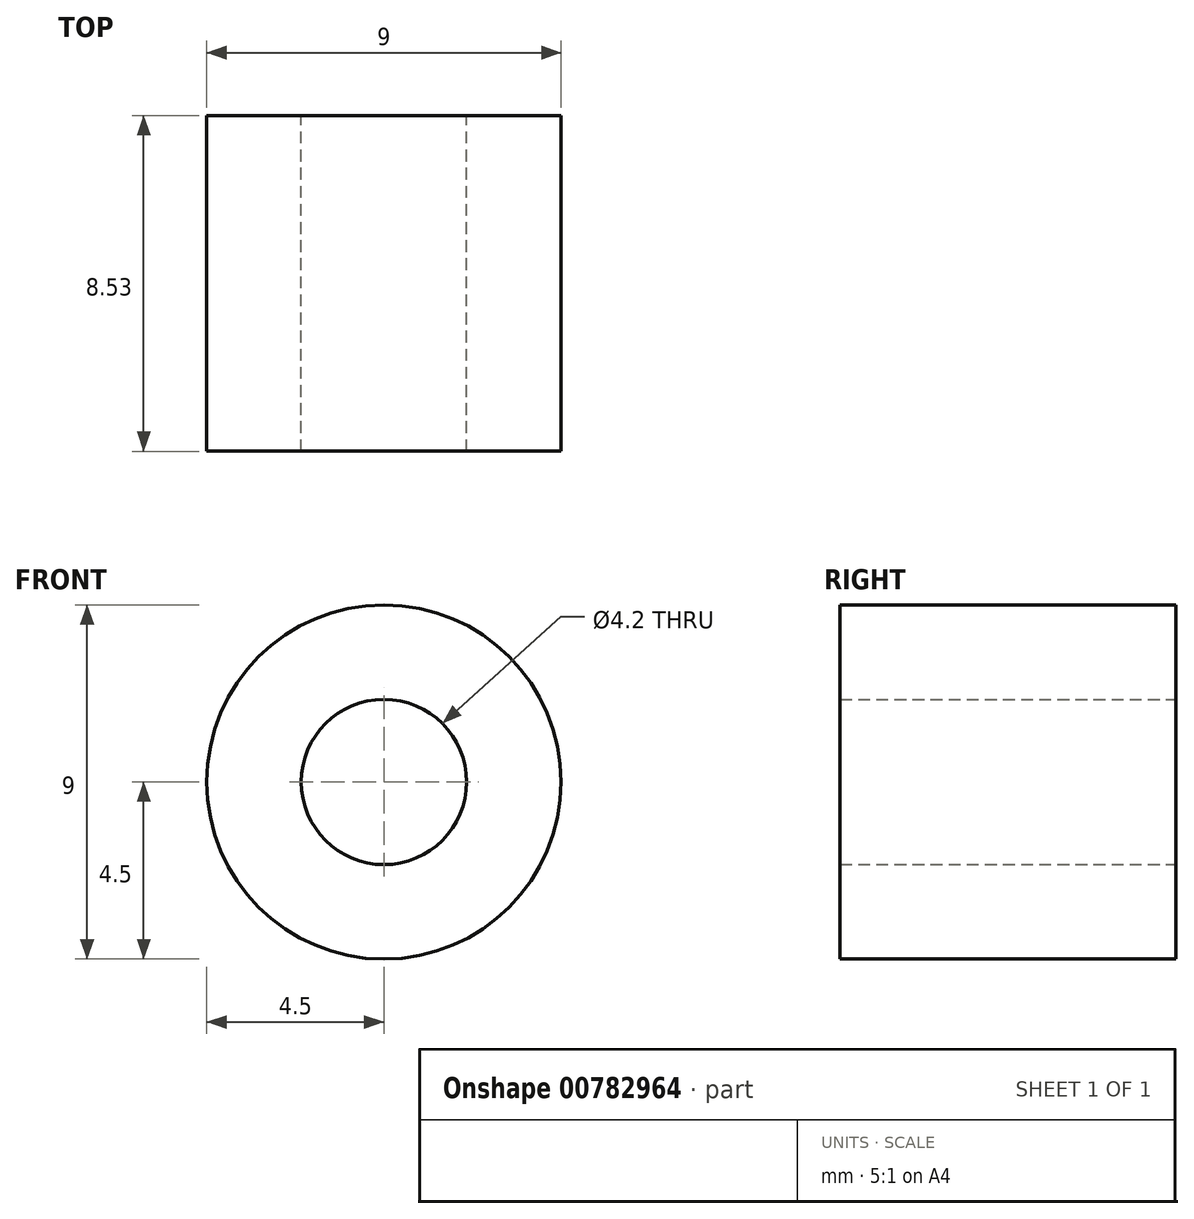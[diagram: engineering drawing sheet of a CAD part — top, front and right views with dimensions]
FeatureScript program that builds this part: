
annotation { "Feature Type Name" : "Feature", "Feature Type Description" : "" }
export const myFeature = defineFeature(function(context is Context, id is Id, definition is map)
    precondition{}
    {
        {
            var Q0;
            Q0=qCreatedBy(makeId("Front.planeOp"),FACE);
            var sketch = newSketch(context, id + "F0", { "sketchPlane" : qUnion([Q0])});
            skCircle(sketch, "E0", {"center": v(0, 0) * mm, "radius": 2.1 * mm});
            skCircle(sketch, "E1", {"center": v(0, 0) * mm, "radius": 4.5 * mm});
            skSolve(sketch);
        }
        {
            var Q0;
            Q0=qSketchRegion(id+"F0",true);
            extrude(context, id + "F1", {"entities" : qUnion([Q0]), "depth" : 8.53 * mm, "offsetDistance" : 25 * mm});
        }
    });
